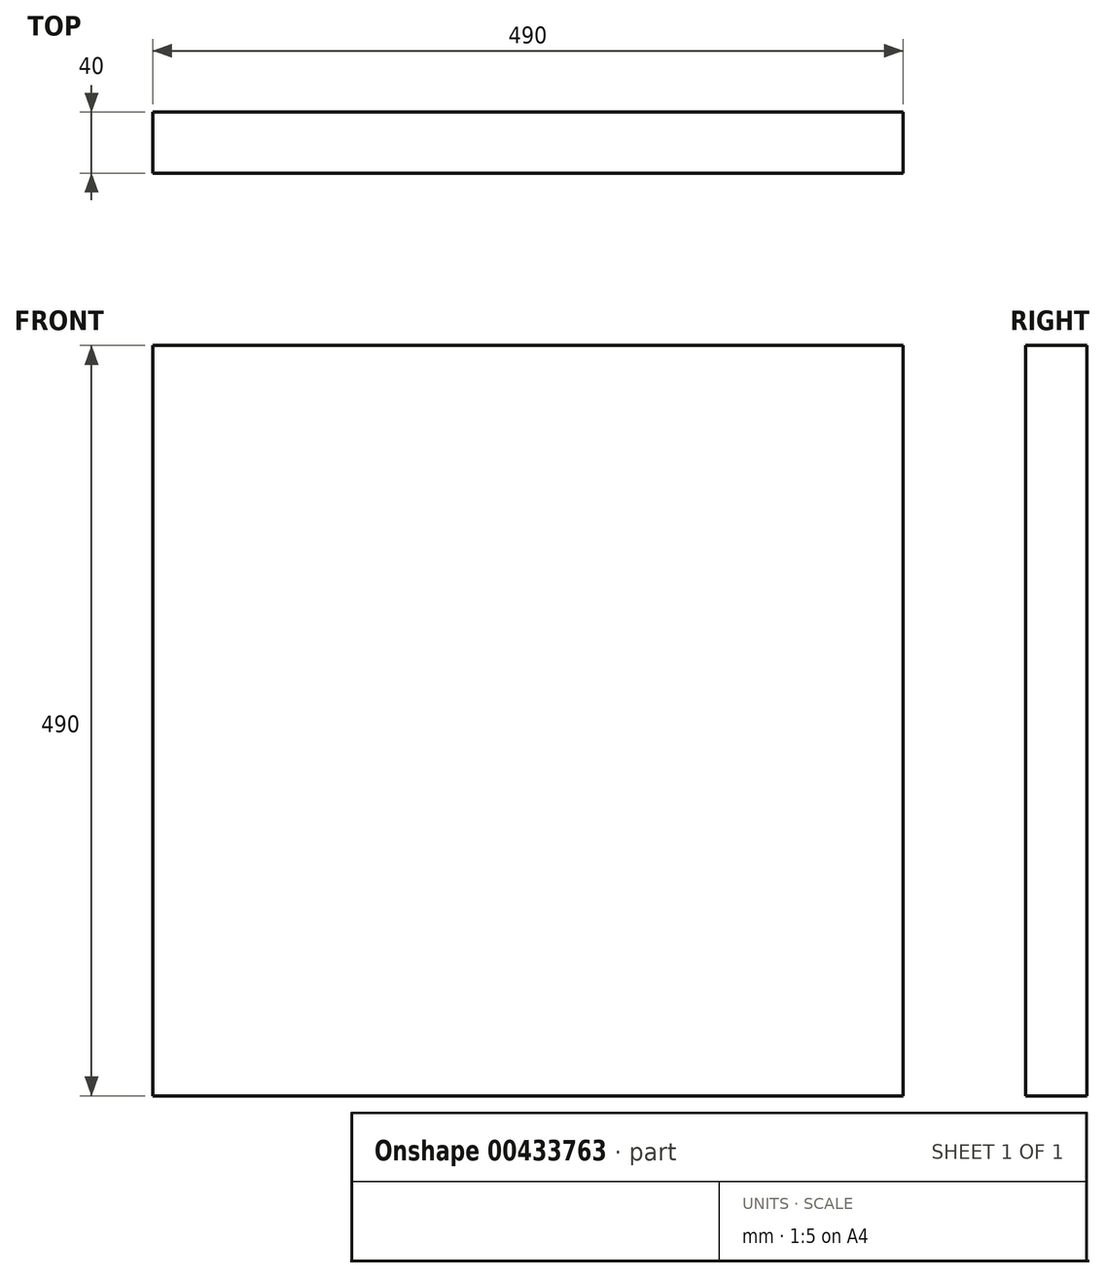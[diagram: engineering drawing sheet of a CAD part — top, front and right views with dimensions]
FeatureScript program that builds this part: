
annotation { "Feature Type Name" : "Feature", "Feature Type Description" : "" }
export const myFeature = defineFeature(function(context is Context, id is Id, definition is map)
    precondition{}
    {
        {
            var Q0;
            Q0=qCreatedBy(makeId("Front.planeOp"),FACE);
            var sketch = newSketch(context, id + "F0", { "sketchPlane" : qUnion([Q0])});
            skLineSegment(sketch, "E0.bottom", {"start": v(245, -245) * mm, "end": v(-245, -245) * mm});
            skLineSegment(sketch, "E0.top", {"start": v(245, 245) * mm, "end": v(-245, 245) * mm});
            skLineSegment(sketch, "E0.left", {"start": v(245, -245) * mm, "end": v(245, 245) * mm});
            skLineSegment(sketch, "E0.right", {"start": v(-245, -245) * mm, "end": v(-245, 245) * mm});
            skPoint(sketch, "E0.middle", {"position": v(0, 0) * mm});
            skSolve(sketch);
        }
        {
            var Q0;
            Q0=makeQuery(id+"F0.imprint","IMPRINT",FACE,{"disambiguationData":[TD([[makeQuery(id+"F0.imprint","IMPRINT",EDGE,{"derivedFrom":sQuery(id+"F0.wireOp",EDGE,"E0.bottom")}),-1.0]])]});
            extrude(context, id + "F1", {"entities" : qUnion([Q0]), "depth" : 40 * mm});
        }
    });
